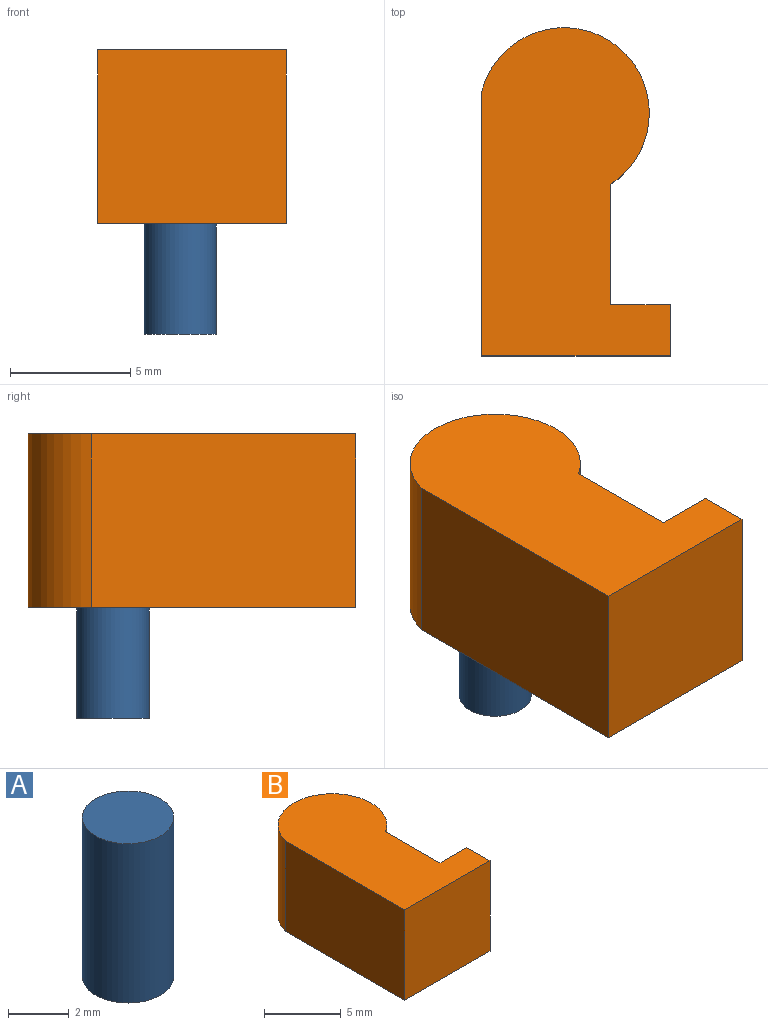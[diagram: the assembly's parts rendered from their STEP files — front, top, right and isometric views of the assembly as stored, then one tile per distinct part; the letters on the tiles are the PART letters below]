
ASSEMBLY  parts=2 mates=1
PART A: 3 faces, bbox 3x3x6.4 mm
  f0: cylinder r=1.5mm len=6.4mm, axis (0,0,-1), area 60.3mm2, adj f1,f2
  f1: plane 3x3mm, normal (0,0,1), area 7.1mm2, adj f0
  f2: plane 3x3mm, normal (0,0,-1), area 7.1mm2, adj f0
PART B: 10 faces, bbox 7.8x13.6x7.2 mm
  f0: plane 7.2x5mm, normal (1,0,0), area 36mm2, adj f1,f5,f6,f7
  f1: cylinder r=3.54mm len=7.2mm, axis (0,0,-1), area 98.8mm2, adj f0,f2,f6,f7
  f2: plane 11x7.2mm, normal (-1,0,0), area 79.2mm2, adj f1,f3,f6,f7
  f3: plane 7.83x7.2mm, normal (0,-1,0), area 56.4mm2, adj f2,f4,f6,f7
  f4: plane 7.2x2.13mm, normal (1,0,0), area 15.3mm2, adj f3,f5,f6,f7
  f5: plane 7.2x2.48mm, normal (0,1,0), area 17.8mm2, adj f0,f4,f6,f7
  f6: plane 13.63x7.83mm, normal (0,0,1), area 82.3mm2, adj f0,f1,f2,f3,f4,f5
  f7: plane 13.63x7.83mm, normal (0,0,-1), area 75.2mm2, adj f0,f1,f2,f3,f4,f5,f8
  f8: cylinder r=1.5mm len=3.6mm, axis (0,0,1), area 33.9mm2, adj f7,f9
  f9: plane 3x3mm, normal (0,0,-1), area 7.1mm2, adj f8
PLACE A t=(6.28,-4.31,14.35)mm
PLACE B t=(2.86,-14.4,19.35)mm
MATE cylindrical A.f0 <-> B.f1  axis (0,0,-1) through (6.28,-4.31,11.15)mm
